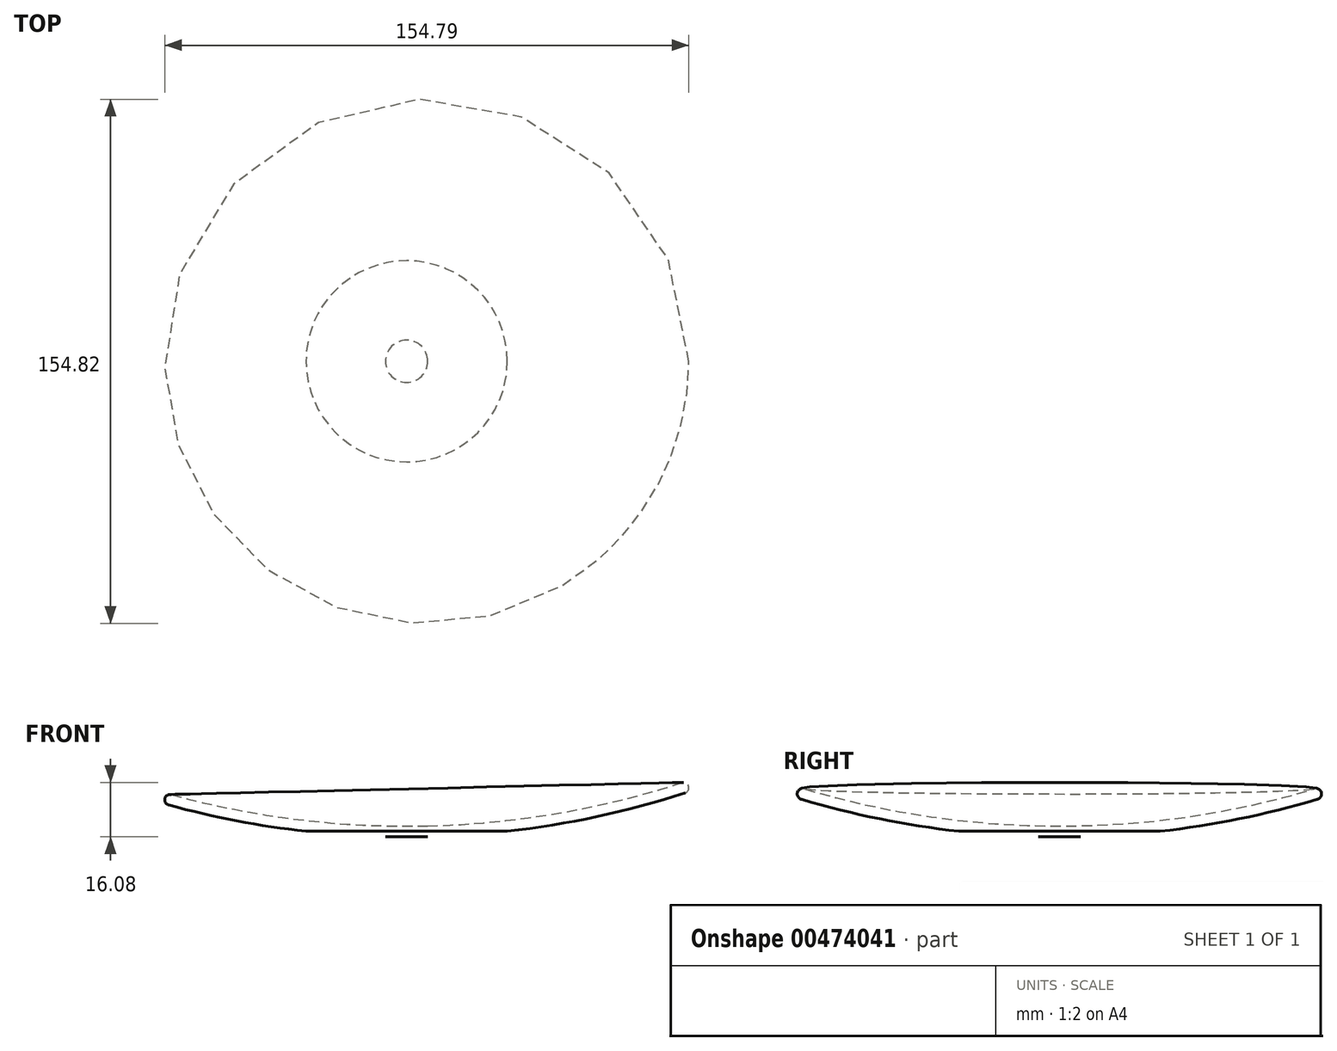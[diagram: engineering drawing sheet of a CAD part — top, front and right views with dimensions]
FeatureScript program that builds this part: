
annotation { "Feature Type Name" : "Feature", "Feature Type Description" : "" }
export const myFeature = defineFeature(function(context is Context, id is Id, definition is map)
    precondition{}
    {
        {
            var Q0;
            Q0=qCreatedBy(makeId("Front.planeOp"),FACE);
            var sketch = newSketch(context, id + "F0", { "sketchPlane" : qUnion([Q0])});
            skArc(sketch, "E0", {"start": v(0, 0) * mm, "mid": v(38.47, 3.7) * mm, "end": v(76, 12.92) * mm});
            skArc(sketch, "E1.0", {"start": v(-0.07, 3.17) * mm, "mid": v(37.94, 6.83) * mm, "end": v(75.02, 15.94) * mm});
            skArc(sketch, "E2", {"start": v(76, 12.92) * mm, "mid": v(77.02, 14.91) * mm, "end": v(75.02, 15.94) * mm});
            skLineSegment(sketch, "E3", {"start": v(-0.07, 3.17) * mm, "end": v(0, 0) * mm});
            skSolve(sketch);
        }
        {
            var Q0;
            Q0=makeQuery(id+"F0.imprint","IMPRINT",FACE,{"disambiguationData":[TD([[makeQuery(id+"F0.imprint","IMPRINT",EDGE,{"derivedFrom":sQuery(id+"F0.wireOp",EDGE,"E0")}),1.0]])]});
            var Q1;
            Q1=sQuery(id+"F0.wireOp",EDGE,"E3");
            revolve(context, id + "F1", {"entities" : qUnion([Q0]), "axis" : qUnion([Q1]), "revolveType" : RevolveType.FULL});
        }
        {
            var Q0;
            Q0=qCreatedBy(makeId("Top.planeOp"),FACE);
            var sketch = newSketch(context, id + "F2", { "sketchPlane" : qUnion([Q0])});
            skCircle(sketch, "E4", {"center": v(0, 0) * mm, "radius": 76.2 * mm});
            skSolve(sketch);
        }
        {
            var Q0;
            Q0=makeQuery(id+"F2.imprint","IMPRINT",FACE,{"disambiguationData":[TD([[makeQuery(id+"F2.imprint","IMPRINT",EDGE,{"derivedFrom":sQuery(id+"F2.wireOp",EDGE,"E4")}),1.0]])]});
            extrude(context, id + "F3", {"entities" : qUnion([Q0]), "operationType" : NewBodyOperationType.REMOVE, "depth" : 1.59 * mm});
        }
    });
